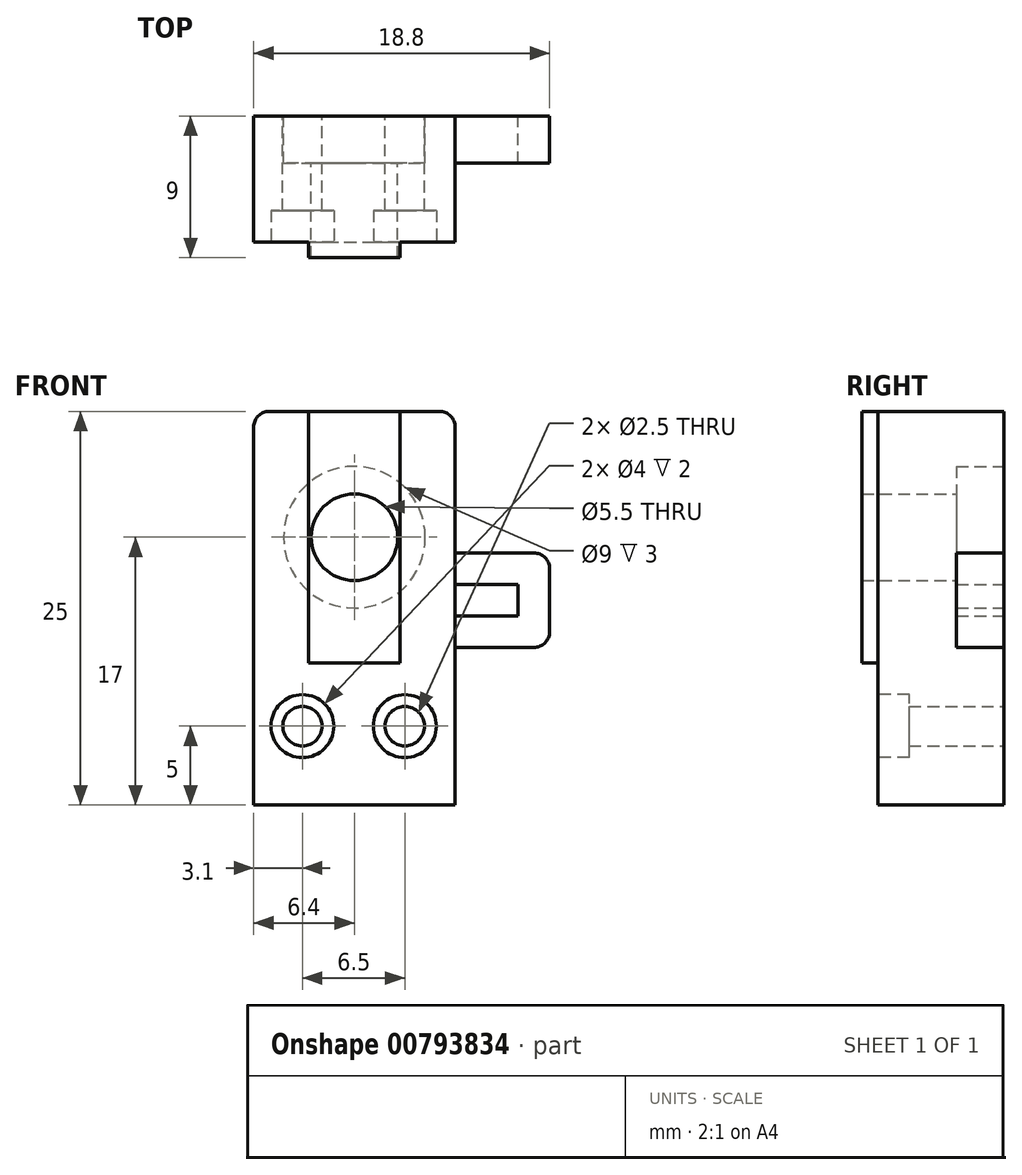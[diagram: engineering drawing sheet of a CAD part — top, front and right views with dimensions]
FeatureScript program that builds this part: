
annotation { "Feature Type Name" : "Feature", "Feature Type Description" : "" }
export const myFeature = defineFeature(function(context is Context, id is Id, definition is map)
    precondition{}
    {
        {
            var Q0;
            Q0=qCreatedBy(makeId("Front.planeOp"),FACE);
            var sketch = newSketch(context, id + "F0", { "sketchPlane" : qUnion([Q0])});
            skLineSegment(sketch, "E0.bottom", {"start": v(-6.4, 3.25) * mm, "end": v(6.4, 3.25) * mm});
            skLineSegment(sketch, "E0.top", {"start": v(-6.4, -3.25) * mm, "end": v(6.4, -3.25) * mm});
            skLineSegment(sketch, "E0.left", {"start": v(-6.4, 3.25) * mm, "end": v(-6.4, -3.25) * mm});
            skLineSegment(sketch, "E0.right", {"start": v(6.4, 3.25) * mm, "end": v(6.4, -3.25) * mm});
            skCircle(sketch, "E1", {"center": v(-3.3, 1.75) * mm, "radius": 1 * mm});
            skCircle(sketch, "E2", {"center": v(3.2, 1.75) * mm, "radius": 1 * mm});
            skPoint(sketch, "E3", {"position": v(0, 3.25) * mm});
            skPoint(sketch, "E4", {"position": v(6.4, 0) * mm});
            skSolve(sketch);
        }
        {
            var Q0;
            Q0=qCreatedBy(makeId("Front.planeOp"),FACE);
            var sketch = newSketch(context, id + "F1", { "sketchPlane" : qUnion([Q0])});
            skLineSegment(sketch, "E5.bottom", {"start": v(-6.4, 21.75) * mm, "end": v(6.4, 21.75) * mm});
            skLineSegment(sketch, "E5.top", {"start": v(-6.4, -3.25) * mm, "end": v(6.4, -3.25) * mm});
            skLineSegment(sketch, "E5.left", {"start": v(-6.4, 21.75) * mm, "end": v(-6.4, -3.25) * mm});
            skLineSegment(sketch, "E5.right", {"start": v(6.4, 21.75) * mm, "end": v(6.4, -3.25) * mm});
            skCircle(sketch, "E6.0", {"center": v(3.2, 1.75) * mm, "radius": 1 * mm, "construction": true});
            skCircle(sketch, "E7.0", {"center": v(-3.3, 1.75) * mm, "radius": 1 * mm, "construction": true});
            skCircle(sketch, "E8", {"center": v(-3.3, 1.75) * mm, "radius": 1.25 * mm});
            skCircle(sketch, "E9", {"center": v(3.2, 1.75) * mm, "radius": 1.25 * mm});
            skSolve(sketch);
        }
        {
            var Q0;
            Q0=qSketchRegion(id+"F1",true);
            extrude(context, id + "F2", {"entities" : qUnion([Q0]), "depth" : 8 * mm, "offsetDistance" : 25 * mm});
        }
        {
            var Q0;
            Q0=makeQuery(id+"F2.opExtrude","CAP_FACE",FACE,{"disambiguationData":[OSD([sQuery(id+"F1.wireOp",EDGE,"E5.bottom"),sQuery(id+"F1.wireOp",EDGE,"E5.top"),sQuery(id+"F1.wireOp",EDGE,"E5.left"),sQuery(id+"F1.wireOp",EDGE,"E5.right"),sQuery(id+"F1.wireOp",EDGE,"E8"),sQuery(id+"F1.wireOp",EDGE,"E9")])],"isStart":true});
            var sketch = newSketch(context, id + "F3", { "sketchPlane" : qUnion([Q0])});
            skCircle(sketch, "E10", {"center": v(0, 13.75) * mm, "radius": 2.75 * mm});
            skSolve(sketch);
        }
        {
            var Q0;
            Q0=qSketchRegion(id+"F3",true);
            extrude(context, id + "F4", {"entities" : qUnion([Q0]), "operationType" : NewBodyOperationType.REMOVE, "endBound" : BoundingType.THROUGH_ALL, "oppositeDirection" : true, "depth" : 25 * mm, "offsetDistance" : 25 * mm});
        }
        {
            var Q0;
            Q0=makeQuery(id+"F2.opExtrude","CAP_FACE",FACE,{"disambiguationData":[OSD([sQuery(id+"F1.wireOp",EDGE,"E5.bottom"),sQuery(id+"F1.wireOp",EDGE,"E5.top"),sQuery(id+"F1.wireOp",EDGE,"E5.left"),sQuery(id+"F1.wireOp",EDGE,"E5.right"),sQuery(id+"F1.wireOp",EDGE,"E8"),sQuery(id+"F1.wireOp",EDGE,"E9")])],"isStart":false});
            var sketch = newSketch(context, id + "F5", { "sketchPlane" : qUnion([Q0])});
            skCircle(sketch, "E11", {"center": v(-3.3, 1.75) * mm, "radius": 2 * mm});
            skCircle(sketch, "E12", {"center": v(3.2, 1.75) * mm, "radius": 2 * mm});
            skSolve(sketch);
        }
        {
            var Q0;
            Q0=qSketchRegion(id+"F5",true);
            extrude(context, id + "F6", {"entities" : qUnion([Q0]), "operationType" : NewBodyOperationType.REMOVE, "oppositeDirection" : true, "depth" : 2 * mm, "offsetDistance" : 25 * mm});
        }
        {
            var Q0;
            Q0=makeQuery(id+"F2.opExtrude","CAP_FACE",FACE,{"disambiguationData":[OSD([sQuery(id+"F1.wireOp",EDGE,"E5.bottom"),sQuery(id+"F1.wireOp",EDGE,"E5.top"),sQuery(id+"F1.wireOp",EDGE,"E5.left"),sQuery(id+"F1.wireOp",EDGE,"E5.right"),sQuery(id+"F1.wireOp",EDGE,"E8"),sQuery(id+"F1.wireOp",EDGE,"E9")])],"isStart":false});
            var sketch = newSketch(context, id + "F7", { "sketchPlane" : qUnion([Q0])});
            skLineSegment(sketch, "E13.bottom", {"start": v(0, 5.75) * mm, "end": v(2.9, 5.75) * mm});
            skLineSegment(sketch, "E13.top", {"start": v(0, 21.75) * mm, "end": v(2.9, 21.75) * mm});
            skLineSegment(sketch, "E13.right", {"start": v(2.9, 5.75) * mm, "end": v(2.9, 21.75) * mm});
            skLineSegment(sketch, "E14.MirrorCS", {"start": v(-2.9, 5.75) * mm, "end": v(-2.9, 21.75) * mm});
            skLineSegment(sketch, "E15.MirrorCS", {"start": v(0, 5.75) * mm, "end": v(-2.9, 5.75) * mm});
            skLineSegment(sketch, "E16.MirrorCS", {"start": v(0, 21.75) * mm, "end": v(-2.9, 21.75) * mm});
            skCircle(sketch, "E17.0", {"center": v(0, 13.75) * mm, "radius": 2.75 * mm});
            skSolve(sketch);
        }
        {
            var Q0;
            Q0=qSketchRegion(id+"F7",true);
            extrude(context, id + "F8", {"entities" : qUnion([Q0]), "operationType" : NewBodyOperationType.ADD, "depth" : 1 * mm, "offsetDistance" : 25 * mm});
        }
        {
            var Q0;
            Q0=makeQuery(id+"F2.opExtrude","SWEPT_FACE",FACE,{"disambiguationData":[OSD([sQuery(id+"F1.wireOp",EDGE,"E5.right")])]});
            var sketch = newSketch(context, id + "F9", { "sketchPlane" : qUnion([Q0])});
            skLineSegment(sketch, "E18.bottom", {"start": v(0, 6.75) * mm, "end": v(-3, 6.75) * mm});
            skLineSegment(sketch, "E18.top", {"start": v(0, 12.75) * mm, "end": v(-3, 12.75) * mm});
            skLineSegment(sketch, "E18.left", {"start": v(0, 6.75) * mm, "end": v(0, 12.75) * mm});
            skLineSegment(sketch, "E18.right", {"start": v(-3, 6.75) * mm, "end": v(-3, 12.75) * mm});
            skSolve(sketch);
        }
        {
            var Q0;
            Q0=qSketchRegion(id+"F9",true);
            extrude(context, id + "F10", {"entities" : qUnion([Q0]), "operationType" : NewBodyOperationType.ADD, "depth" : 6 * mm, "offsetDistance" : 25 * mm});
        }
        {
            var Q0;
            Q0=makeQuery(id+"F10.boolean.opBoolean","MERGE",FACE,{"derivedFrom":[makeQuery(id+"F2.opExtrude","CAP_FACE",FACE,{"disambiguationData":[OSD([sQuery(id+"F1.wireOp",EDGE,"E5.bottom"),sQuery(id+"F1.wireOp",EDGE,"E5.top"),sQuery(id+"F1.wireOp",EDGE,"E5.left"),sQuery(id+"F1.wireOp",EDGE,"E5.right"),sQuery(id+"F1.wireOp",EDGE,"E8"),sQuery(id+"F1.wireOp",EDGE,"E9")])],"isStart":true}),makeQuery(id+"F10.opExtrude","SWEPT_FACE",FACE,{"disambiguationData":[OSD([sQuery(id+"F9.wireOp",EDGE,"E18.left")])]})]});
            var sketch = newSketch(context, id + "F11", { "sketchPlane" : qUnion([Q0])});
            skLineSegment(sketch, "E19.bottom", {"start": v(-10.4, 10.75) * mm, "end": v(-6.4, 10.75) * mm});
            skLineSegment(sketch, "E19.top", {"start": v(-10.4, 8.75) * mm, "end": v(-6.4, 8.75) * mm});
            skLineSegment(sketch, "E19.left", {"start": v(-10.4, 10.75) * mm, "end": v(-10.4, 8.75) * mm});
            skLineSegment(sketch, "E19.right", {"start": v(-6.4, 10.75) * mm, "end": v(-6.4, 8.75) * mm});
            skSolve(sketch);
        }
        {
            var Q0;
            Q0=qSketchRegion(id+"F11",true);
            var Q1;
            Q1=makeQuery(id+"F10.opExtrude","SWEPT_FACE",FACE,{"disambiguationData":[OSD([sQuery(id+"F9.wireOp",EDGE,"E18.right")])]});
            extrude(context, id + "F12", {"entities" : qUnion([Q0]), "operationType" : NewBodyOperationType.REMOVE, "endBound" : BoundingType.UP_TO_SURFACE, "oppositeDirection" : true, "depth" : 25 * mm, "endBoundEntityFace" : qUnion([Q1]), "offsetDistance" : 25 * mm});
        }
        {
            var Q0;
            Q0=makeQuery(id+"F10.opExtrude","CAP_EDGE",EDGE,{"disambiguationData":[OSD([sQuery(id+"F9.wireOp",EDGE,"E18.bottom")])],"isStart":false});
            var Q1;
            Q1=makeQuery(id+"F10.opExtrude","CAP_EDGE",EDGE,{"disambiguationData":[OSD([sQuery(id+"F9.wireOp",EDGE,"E18.top")])],"isStart":false});
            var Q2;
            Q2=makeQuery(id+"F2.opExtrude","SWEPT_EDGE",EDGE,{"disambiguationData":[OSD([sQuery(id+"F1.wireOp",EDGE,"E5.bottom"),sQuery(id+"F1.wireOp",EDGE,"E5.right")])]});
            var Q3;
            Q3=makeQuery(id+"F2.opExtrude","SWEPT_EDGE",EDGE,{"disambiguationData":[OSD([sQuery(id+"F1.wireOp",EDGE,"E5.bottom"),sQuery(id+"F1.wireOp",EDGE,"E5.left")])]});
            var Q4;
            Q4=makeQuery(id+"F10.opExtrude","CAP_EDGE",EDGE,{"disambiguationData":[OSD([sQuery(id+"F9.wireOp",EDGE,"E18.right")])],"isStart":true});
            fillet(context, id + "F13", {"entities" : qUnion([Q0, Q1, Q2, Q3, Q4]), "radius" : 1 * mm, "tangentPropagation" : true, "allowEdgeOverflow" : false});
        }
        {
            var Q0;
            Q0=makeQuery(id+"F10.boolean.opBoolean","MERGE",FACE,{"derivedFrom":[makeQuery(id+"F2.opExtrude","CAP_FACE",FACE,{"disambiguationData":[OSD([sQuery(id+"F1.wireOp",EDGE,"E5.bottom"),sQuery(id+"F1.wireOp",EDGE,"E5.top"),sQuery(id+"F1.wireOp",EDGE,"E5.left"),sQuery(id+"F1.wireOp",EDGE,"E5.right"),sQuery(id+"F1.wireOp",EDGE,"E8"),sQuery(id+"F1.wireOp",EDGE,"E9")])],"isStart":true}),makeQuery(id+"F10.opExtrude","SWEPT_FACE",FACE,{"disambiguationData":[OSD([sQuery(id+"F9.wireOp",EDGE,"E18.left")])]})]});
            var sketch = newSketch(context, id + "F14", { "sketchPlane" : qUnion([Q0])});
            skCircle(sketch, "E20", {"center": v(0, 13.75) * mm, "radius": 4.5 * mm});
            skSolve(sketch);
        }
        {
            var Q0;
            Q0=qSketchRegion(id+"F14",true);
            extrude(context, id + "F15", {"entities" : qUnion([Q0]), "operationType" : NewBodyOperationType.REMOVE, "oppositeDirection" : true, "depth" : 3 * mm, "offsetDistance" : 25 * mm});
        }
    });
